# Revit family: ledhighbay-b_150w-840-w_545001078200
name_source: partatom
category: Lighting Fixtures
units: mm (PartAtom-declared; Revit-internal decimal feet)

## family parameters
Cut with Voids When Loaded = No
Host = Face
Light Source = No
Part Type = Normal
Room Calculation Point = No
Round Connector Dimension = Use Diameter
Shared = No

## types (1)
- LEDHighbay-B 150W-840-W (1 x LED, 19500 lm, 4000)
    Apparent Load = 150 VA
    Approval mark = CE
    CIE Flux Codes = 57 86 98 100 100
    Color Rendering = 80
    Color Temperature = 4000
    Control Gear = Electronic ballast
    Default Elevation = 1800 mm
    Description = Highbay Basic 150W-19500lm-4000K-90°-Black-IP65
    Frequency = 60 Hz
    Height = 78 mm  [stored 0.255906 ft]
    Lamp = 1 x LED
    Lamp Light Flux = 19500 lm
    Lamp count = 1
    Length = 291 mm
    Luminous efficacy = 130 lm/W
    Manufacturer = OPPLE
    ModVariant = No
    Model = 545001078200
    Mounting Place = Ceiling
    Mounting Type = Pendant
    Number of Poles = 1
    OnlyDefault = Yes
    Power Factor = 1
    Product Name = LEDHighbay-B 150W-840-W
    Product group = Pendant luminaire
    ProductGroupID = 9
    Protection Class = Protection class I
    Protection Degree = IP 65
    RLX_Detail_Level = 1
    RLX_Emergency_Light_Flux = 0 lm
    RLX_Emergency_Type = 0
    RLX_Emergency_Type_DB = No
    RlxData = <blob elided: 312349 chars, md5=35d7d623>
    Socket = socket
    Standby Power = 0 W
    System Light Flux = 19500 lm
    System Power = 150 W
    Type Comments = Product without accessories
    Type Image = web_hb_b1_120w_150w.jpg
    URL = http://relux.com
    VarID = ---
    Voltage = 230 V
    Voltage Range = 220-240 V
    Weight = 0.00 kg
    Width = 291 mm

note: [stored X ft] marks values corroborated as IEEE doubles in the binary element streams (Revit-internal decimal feet)

## geometry (parser evidence)
native form markers: Sweep x11
no freeform markers — native parametric forms only
